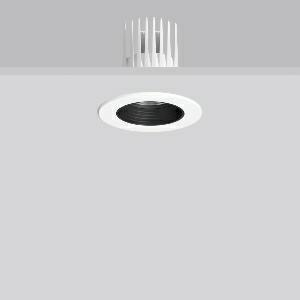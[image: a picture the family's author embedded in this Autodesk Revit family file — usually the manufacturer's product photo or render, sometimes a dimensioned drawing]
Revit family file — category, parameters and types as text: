
# Revit family: heledon_mini_e_901755_002_3_76_e0b7
name_source: partatom
category: Lighting Fixtures
units: mm (PartAtom-declared; Revit-internal decimal feet)

## family parameters
Cut with Voids When Loaded = No
Host = Face
Light Source = No
Part Type = Normal
Room Calculation Point = No
Round Connector Dimension = Use Diameter
Shared = No

## types (1)
- HELEDON mini E (1 x LED Modul 935, 2800 lm, 3500)
    Apparent Load = 29 VA
    Approval mark = CE
    CIE Flux Codes = 95 100 100 100 100
    Color Rendering = 92
    Color Temperature = 3500
    Default Elevation = 1800 mm
    Description = Series: HELEDON mini
Round recessed downlight. Housing: die-cast aluminium, powder-coated. Black plastic ring and recessed LED to prevent glare from the side. Optical assembly with lens made of plastic (polycarbonate) for the best homogeneous light distribution - can be changed without tools. Best colour rendering index Ra>90. Suitable for Recessed ceiling mounting. Installation without tools thanks to spring fastening system. Including separate LED converter with connecting cable 600 mm.High quality converter without flickering and stroboscopic effect. Through-wiring box (5 pole) available as accessory. The following accessories can be mounted without use of tools: interchangeable lenses, decorative glasses, honeycomb louvre, clear and frosted diffusers, white interchangeable plastic ring. 
Colour: traffic white, matt (RAL 9016)
Diameter: 124 mm
Height: 3 mm
Cut-out diameter: 114 mm
Recess height: 170 mm
Luminaire: recess height: 120 mm
Lamp: LED
Socket: without socket
Colour temperature: 3500K
Colour rendering index (CRI): 92
System power: 29 W
Rated luminous flux: 2800 lm
Luminous efficiency: 97 lm/W
Control gear: Converter, dimmable, DALI
Protection class: II
Type of protection: IP 20
    Height = 0 mm  [stored 0 ft]
    Lamp = 1 x LED Modul 935
    Lamp Light Flux = 2800 lm
    Lamp count = 1
    Length = 124 mm  [stored 0.406824 ft]
    Lifetime = 50000 h
    Luminous efficacy = 97 lm/W
    Manufacturer = RZB
    ModVariant = No
    Model = 901755.002.3.76
    Mounting Place = Ceiling
    Mounting Type = Recessed
    Number of Poles = 1
    OnlyDefault = Yes
    Power Factor = 1
    Product Name = HELEDON mini E
    Product group = Recessed downlights
    ProductGroupID = 402
    Protection Class = Protection class II
    Protection Degree = IP 20
    RLX_Detail_Level = 1
    RLX_Emergency_Light_Flux = 0 lm
    RLX_Emergency_Type = 0
    RLX_Emergency_Type_DB = No
    RlxData = <blob elided: 132769 chars, md5=ba6574c6>
    Socket = socket
    Standby Power = 0 W
    System Light Flux = 2800 lm
    System Power = 29 W
    Type Comments = Product without accessories
    Type Image = 901656.002.jpg
    URL = http://relux.com
    VarID = ---
    Voltage = 230 V
    Voltage Range = 220-240 V
    Weight = 0.00 kg
    Width = 0 mm  [stored 0 ft]

note: [stored X ft] marks values corroborated as IEEE doubles in the binary element streams (Revit-internal decimal feet)

## geometry (parser evidence)
native form markers: Blend x4, Sweep x11
no freeform markers — native parametric forms only
